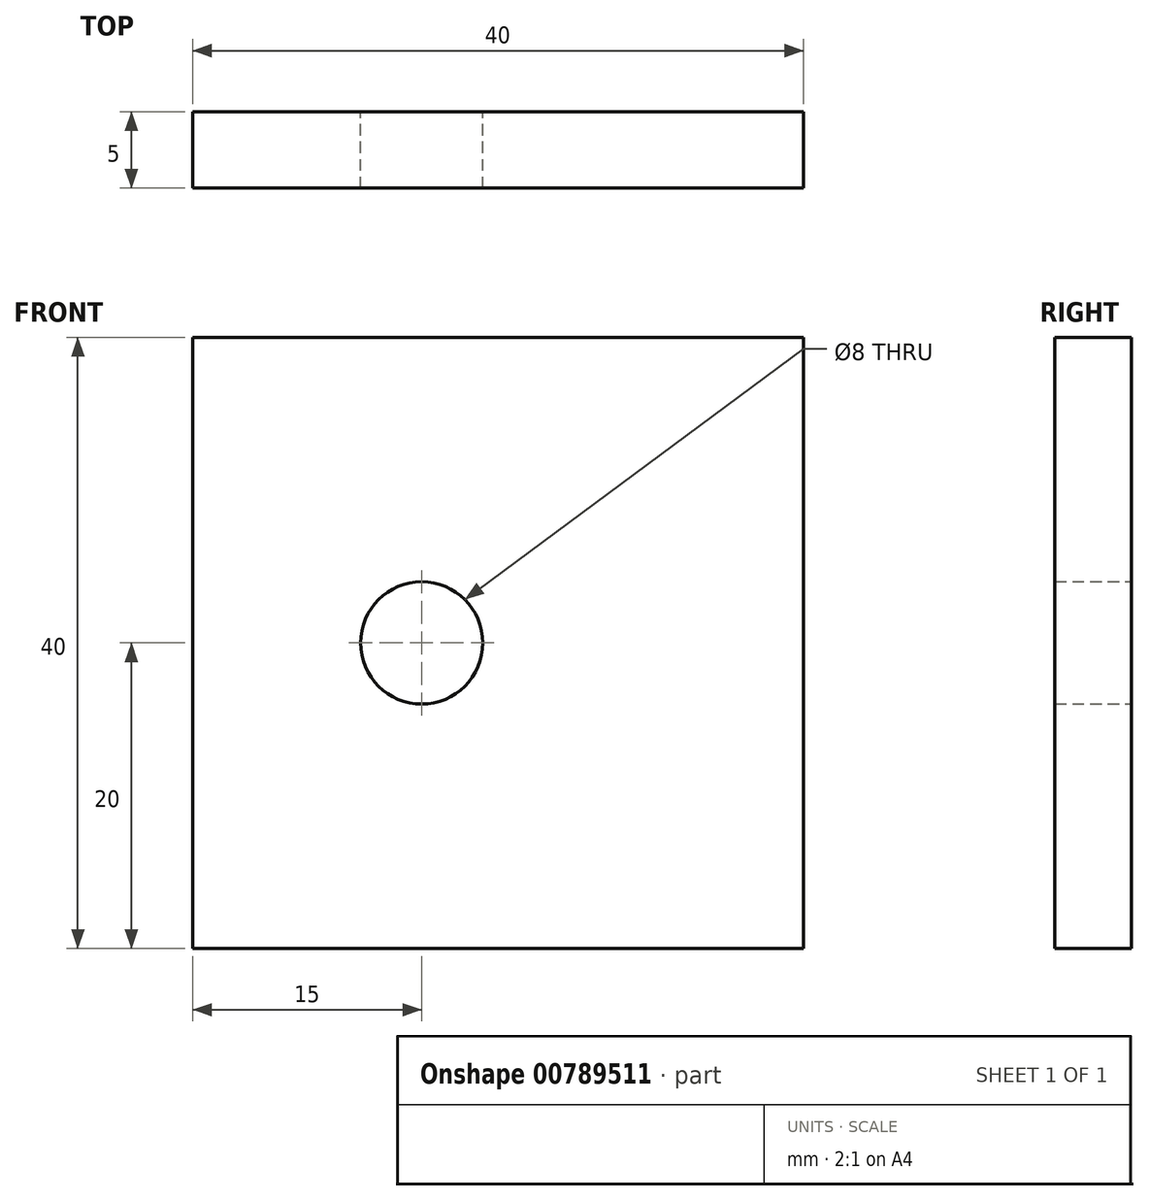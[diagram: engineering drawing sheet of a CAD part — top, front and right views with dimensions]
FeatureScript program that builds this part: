
annotation { "Feature Type Name" : "Feature", "Feature Type Description" : "" }
export const myFeature = defineFeature(function(context is Context, id is Id, definition is map)
    precondition{}
    {
        {
            var Q0;
            Q0=qCreatedBy(makeId("Front.planeOp"),FACE);
            var sketch = newSketch(context, id + "F0", { "sketchPlane" : qUnion([Q0])});
            skLineSegment(sketch, "E0.bottom", {"start": v(0, 0) * mm, "end": v(40, 0) * mm});
            skLineSegment(sketch, "E0.top", {"start": v(0, 40) * mm, "end": v(40, 40) * mm});
            skLineSegment(sketch, "E0.left", {"start": v(0, 0) * mm, "end": v(0, 40) * mm});
            skLineSegment(sketch, "E0.right", {"start": v(40, 0) * mm, "end": v(40, 40) * mm});
            skLineSegment(sketch, "E1", {"start": v(0, 20) * mm, "end": v(15, 20) * mm, "construction": true});
            skCircle(sketch, "E2", {"center": v(15, 20) * mm, "radius": 4 * mm});
            skSolve(sketch);
        }
        {
            var Q0;
            Q0 = qSketchRegion(id + "F0", true);
            extrude(context, id + "F1", {"entities" : qUnion([Q0]), "depth" : 5 * mm, "offsetDistance" : 25 * mm});
        }
    });
